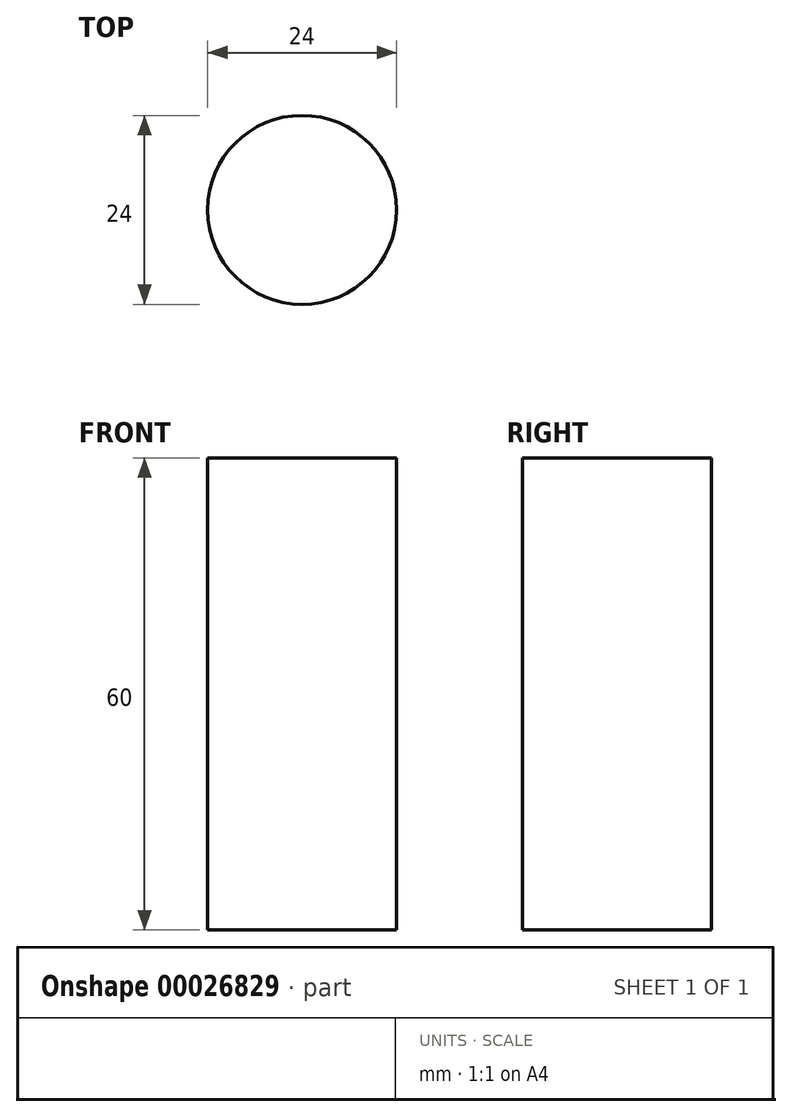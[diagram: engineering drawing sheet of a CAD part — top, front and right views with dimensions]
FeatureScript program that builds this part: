
annotation { "Feature Type Name" : "Feature", "Feature Type Description" : "" }
export const myFeature = defineFeature(function(context is Context, id is Id, definition is map)
    precondition{}
    {
        {
            var Q0;
            Q0=qCreatedBy(makeId("Top.planeOp"),FACE);
            var sketch = newSketch(context, id + "F0", { "sketchPlane" : qUnion([Q0])});
            skCircle(sketch, "E0", {"center": v(0, 0) * mm, "radius": 12 * mm});
            skSolve(sketch);
        }
        {
            var Q0;
            Q0=makeQuery(id+"F0.imprint","IMPRINT",FACE,{"disambiguationData":[TD([[makeQuery(id+"F0.imprint","IMPRINT",EDGE,{"derivedFrom":sQuery(id+"F0.wireOp",EDGE,"E0")}),1.0]])]});
            extrude(context, id + "F1", {"entities" : qUnion([Q0]), "depth" : 60 * mm});
        }
    });
